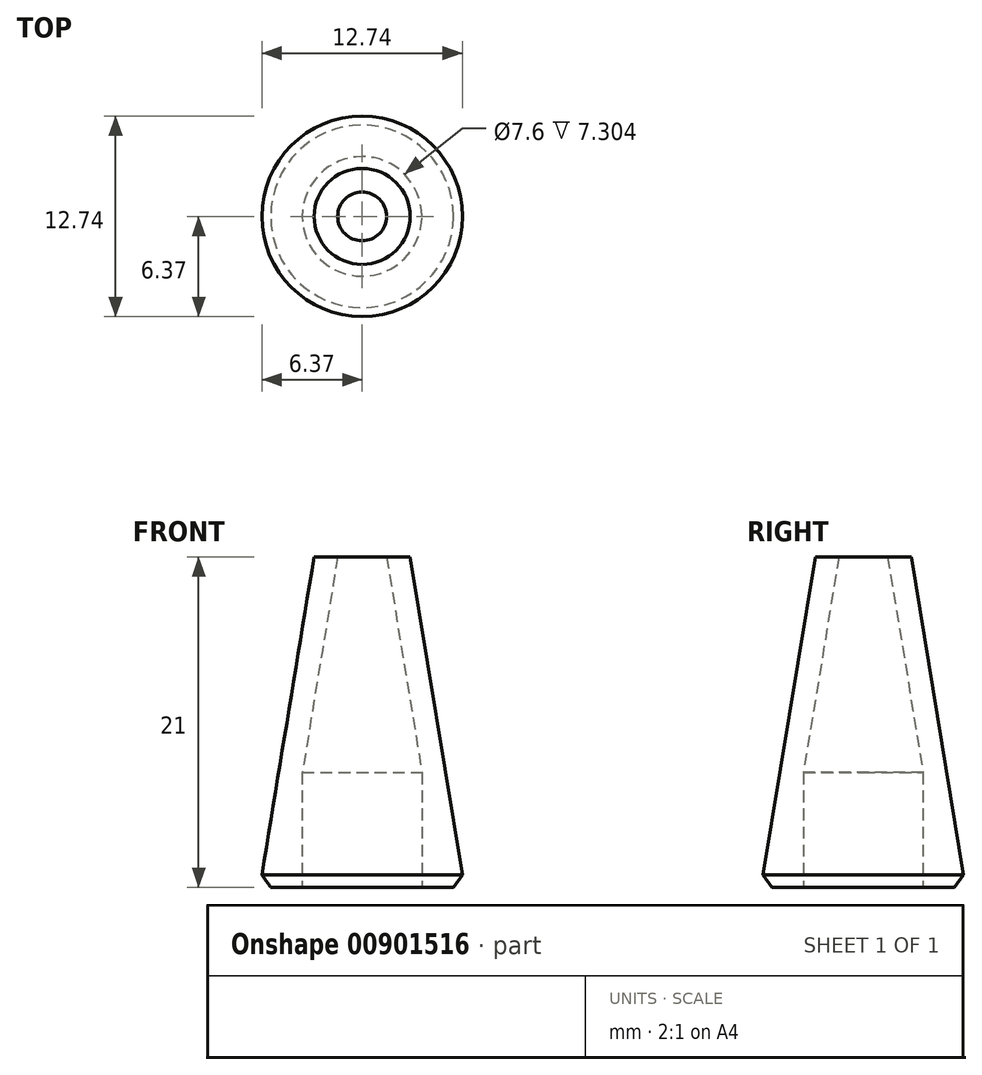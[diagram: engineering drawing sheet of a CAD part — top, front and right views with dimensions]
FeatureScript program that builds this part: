
annotation { "Feature Type Name" : "Feature", "Feature Type Description" : "" }
export const myFeature = defineFeature(function(context is Context, id is Id, definition is map)
    precondition{}
    {
        {
            var Q0;
            Q0=qCreatedBy(makeId("Front.planeOp"),FACE);
            var sketch = newSketch(context, id + "F0", { "sketchPlane" : qUnion([Q0])});
            skLineSegment(sketch, "E0", {"start": v(-5, 0) * mm, "end": v(-6.5, 0) * mm});
            skLineSegment(sketch, "E1", {"start": v(-6.5, 0) * mm, "end": v(-3.05, 21) * mm});
            skLineSegment(sketch, "E2", {"start": v(-3.05, 21) * mm, "end": v(-1.55, 21) * mm});
            skLineSegment(sketch, "E3", {"start": v(-1.55, 21) * mm, "end": v(-5, 0) * mm});
            skPoint(sketch, "E4", {"position": v(-5.8, 0) * mm});
            skPoint(sketch, "E5", {"position": v(-6.37, 0.8) * mm});
            skLineSegment(sketch, "E6", {"start": v(-5.8, 0) * mm, "end": v(-6.37, 0.8) * mm});
            skLineSegment(sketch, "E7", {"start": v(-5, 0) * mm, "end": v(-3.8, 0) * mm});
            skLineSegment(sketch, "E8", {"start": v(-3.8, 0) * mm, "end": v(-3.8, 7.3) * mm});
            skSolve(sketch);
        }
        {
            var Q0;
            Q0=qCreatedBy(makeId("Front.planeOp"),FACE);
            var sketch = newSketch(context, id + "F1", { "sketchPlane" : qUnion([Q0])});
            skLineSegment(sketch, "E9", {"start": v(0, 0) * mm, "end": v(0, 21.14) * mm});
            skSolve(sketch);
        }
        {
            var Q0;
            {var subQ0=sQuery(id+"F0.wireOp",EDGE,"E2");Q0=makeQuery(id+"F0.imprint","IMPRINT",FACE,{"disambiguationData":[TD([[makeQuery(id+"F0.imprint","IMPRINT",EDGE,{"derivedFrom":subQ0}),-1.0]])]});}
            var Q1;
            {var subQ0=sQuery(id+"F0.wireOp",EDGE,"E7");Q1=makeQuery(id+"F0.imprint","IMPRINT",FACE,{"disambiguationData":[TD([[makeQuery(id+"F0.imprint","IMPRINT",EDGE,{"derivedFrom":subQ0}),1.0]])]});}
            var Q2;
            Q2=sQuery(id+"F1.wireOp",EDGE,"E9");
            revolve(context, id + "F2", {"surfaceOperationType" : NewSurfaceOperationType.NEW, "entities" : qUnion([Q0, Q1]), "axis" : qUnion([Q2]), "revolveType" : RevolveType.FULL});
        }
    });
